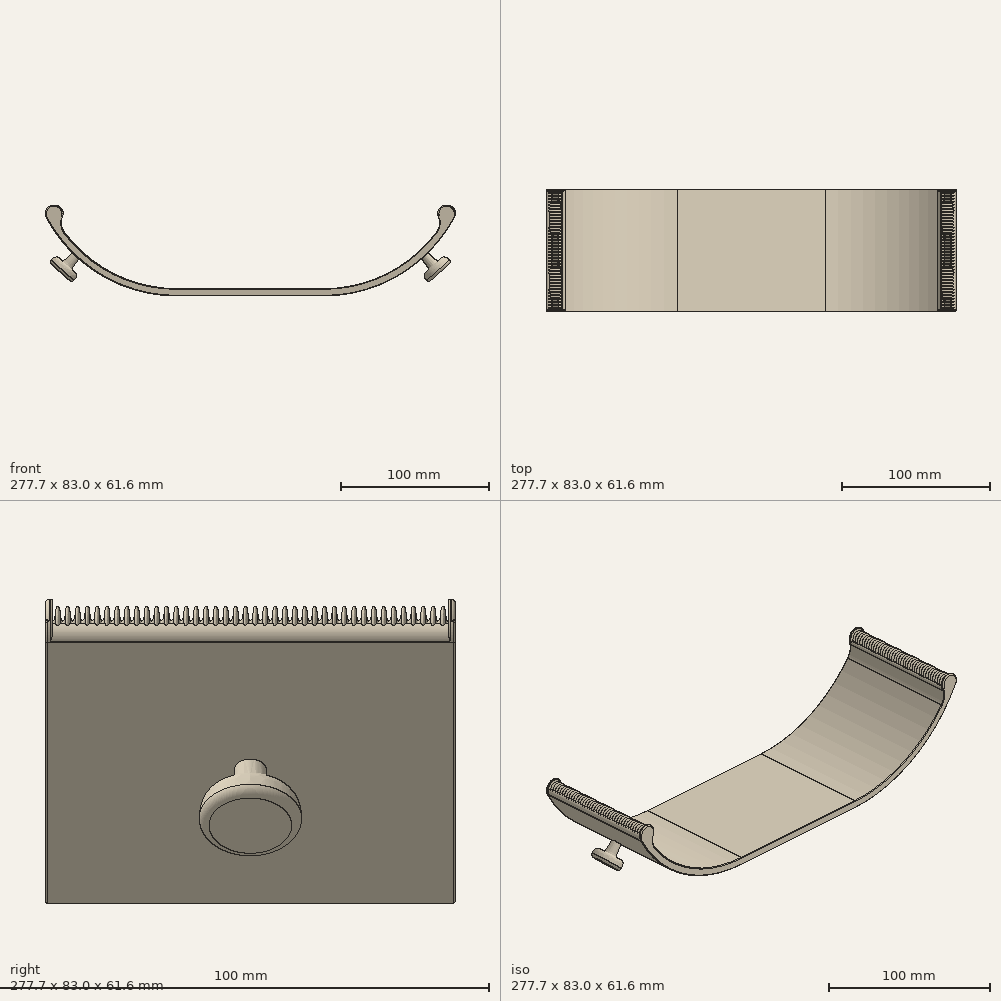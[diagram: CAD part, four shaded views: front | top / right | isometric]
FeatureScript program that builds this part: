
annotation { "Feature Type Name" : "Feature", "Feature Type Description" : "" }
export const myFeature = defineFeature(function(context is Context, id is Id, definition is map)
    precondition{}
    {
        {
            var Q0;
            Q0=qCreatedBy(makeId("Right.planeOp"),FACE);
            var sketch = newSketch(context, id + "F0", { "sketchPlane" : qUnion([Q0])});
            skLineSegment(sketch, "E0", {"start": v(1.5, 1.6) * mm, "end": v(1.5, 5.6) * mm});
            skLineSegment(sketch, "E1", {"start": v(1.1, 6) * mm, "end": v(0.8, 6) * mm});
            skLineSegment(sketch, "E2", {"start": v(0, 5.2) * mm, "end": v(0, 0) * mm});
            skLineSegment(sketch, "E3.top", {"start": v(81.9, 6) * mm, "end": v(82.2, 6) * mm});
            skLineSegment(sketch, "E3.right", {"start": v(83, 0) * mm, "end": v(83, 5.2) * mm});
            skArc(sketch, "E4.filletArc", {"start": v(81.9, 6) * mm, "mid": v(81.62, 5.88) * mm, "end": v(81.5, 5.6) * mm});
            skPoint(sketch, "E5.visualSharp", {"position": v(83, 6) * mm});
            skArc(sketch, "E5.filletArc", {"start": v(83, 5.2) * mm, "mid": v(82.77, 5.77) * mm, "end": v(82.2, 6) * mm});
            skArc(sketch, "E6.filletArc", {"start": v(1.5, 5.6) * mm, "mid": v(1.38, 5.88) * mm, "end": v(1.1, 6) * mm});
            skArc(sketch, "E7.filletArc", {"start": v(0.8, 6) * mm, "mid": v(0.23, 5.77) * mm, "end": v(0, 5.2) * mm});
            skEllipticalArc(sketch, "E8", {});
            skEllipticalArc(sketch, "E9", {});
            skEllipticalArc(sketch, "E10.MirrorCS", {});
            skEllipticalArc(sketch, "E11.MirrorCS", {});
            skLineSegment(sketch, "E12", {"start": v(81.5, 1.6) * mm, "end": v(81.5, 5.6) * mm});
            skEllipticalArc(sketch, "E13.1.0.0", {});
            skEllipticalArc(sketch, "E13.1.0.1", {});
            skEllipticalArc(sketch, "E13.1.0.2", {});
            skEllipticalArc(sketch, "E13.1.0.3", {});
            skEllipticalArc(sketch, "E13.2.0.0", {});
            skEllipticalArc(sketch, "E13.2.0.1", {});
            skEllipticalArc(sketch, "E13.2.0.2", {});
            skEllipticalArc(sketch, "E13.2.0.3", {});
            skEllipticalArc(sketch, "E13.3.0.0", {});
            skEllipticalArc(sketch, "E13.3.0.1", {});
            skEllipticalArc(sketch, "E13.3.0.2", {});
            skEllipticalArc(sketch, "E13.3.0.3", {});
            skEllipticalArc(sketch, "E13.4.0.0", {});
            skEllipticalArc(sketch, "E13.4.0.1", {});
            skEllipticalArc(sketch, "E13.4.0.2", {});
            skEllipticalArc(sketch, "E13.4.0.3", {});
            skEllipticalArc(sketch, "E13.5.0.0", {});
            skEllipticalArc(sketch, "E13.5.0.1", {});
            skEllipticalArc(sketch, "E13.5.0.2", {});
            skEllipticalArc(sketch, "E13.5.0.3", {});
            skEllipticalArc(sketch, "E13.6.0.0", {});
            skEllipticalArc(sketch, "E13.6.0.1", {});
            skEllipticalArc(sketch, "E13.6.0.2", {});
            skEllipticalArc(sketch, "E13.6.0.3", {});
            skEllipticalArc(sketch, "E13.7.0.0", {});
            skEllipticalArc(sketch, "E13.7.0.1", {});
            skEllipticalArc(sketch, "E13.7.0.2", {});
            skEllipticalArc(sketch, "E13.7.0.3", {});
            skEllipticalArc(sketch, "E13.8.0.0", {});
            skEllipticalArc(sketch, "E13.8.0.1", {});
            skEllipticalArc(sketch, "E13.8.0.2", {});
            skEllipticalArc(sketch, "E13.8.0.3", {});
            skEllipticalArc(sketch, "E13.9.0.0", {});
            skEllipticalArc(sketch, "E13.9.0.1", {});
            skEllipticalArc(sketch, "E13.9.0.2", {});
            skEllipticalArc(sketch, "E13.9.0.3", {});
            skEllipticalArc(sketch, "E13.10.0.0", {});
            skEllipticalArc(sketch, "E13.10.0.1", {});
            skEllipticalArc(sketch, "E13.10.0.2", {});
            skEllipticalArc(sketch, "E13.10.0.3", {});
            skEllipticalArc(sketch, "E13.11.0.0", {});
            skEllipticalArc(sketch, "E13.11.0.1", {});
            skEllipticalArc(sketch, "E13.11.0.2", {});
            skEllipticalArc(sketch, "E13.11.0.3", {});
            skEllipticalArc(sketch, "E13.12.0.0", {});
            skEllipticalArc(sketch, "E13.12.0.1", {});
            skEllipticalArc(sketch, "E13.12.0.2", {});
            skEllipticalArc(sketch, "E13.12.0.3", {});
            skEllipticalArc(sketch, "E13.13.0.0", {});
            skEllipticalArc(sketch, "E13.13.0.1", {});
            skEllipticalArc(sketch, "E13.13.0.2", {});
            skEllipticalArc(sketch, "E13.13.0.3", {});
            skEllipticalArc(sketch, "E13.14.0.0", {});
            skEllipticalArc(sketch, "E13.14.0.1", {});
            skEllipticalArc(sketch, "E13.14.0.2", {});
            skEllipticalArc(sketch, "E13.14.0.3", {});
            skEllipticalArc(sketch, "E13.15.0.0", {});
            skEllipticalArc(sketch, "E13.15.0.1", {});
            skEllipticalArc(sketch, "E13.15.0.2", {});
            skEllipticalArc(sketch, "E13.15.0.3", {});
            skEllipticalArc(sketch, "E13.16.0.0", {});
            skEllipticalArc(sketch, "E13.16.0.1", {});
            skEllipticalArc(sketch, "E13.16.0.2", {});
            skEllipticalArc(sketch, "E13.16.0.3", {});
            skEllipticalArc(sketch, "E13.17.0.0", {});
            skEllipticalArc(sketch, "E13.17.0.1", {});
            skEllipticalArc(sketch, "E13.17.0.2", {});
            skEllipticalArc(sketch, "E13.17.0.3", {});
            skEllipticalArc(sketch, "E13.18.0.0", {});
            skEllipticalArc(sketch, "E13.18.0.1", {});
            skEllipticalArc(sketch, "E13.18.0.2", {});
            skEllipticalArc(sketch, "E13.18.0.3", {});
            skEllipticalArc(sketch, "E13.19.0.0", {});
            skEllipticalArc(sketch, "E13.19.0.1", {});
            skEllipticalArc(sketch, "E13.19.0.2", {});
            skEllipticalArc(sketch, "E13.19.0.3", {});
            skEllipticalArc(sketch, "E13.20.0.0", {});
            skEllipticalArc(sketch, "E13.20.0.1", {});
            skEllipticalArc(sketch, "E13.20.0.2", {});
            skEllipticalArc(sketch, "E13.20.0.3", {});
            skEllipticalArc(sketch, "E13.21.0.0", {});
            skEllipticalArc(sketch, "E13.21.0.1", {});
            skEllipticalArc(sketch, "E13.21.0.2", {});
            skEllipticalArc(sketch, "E13.21.0.3", {});
            skEllipticalArc(sketch, "E13.22.0.0", {});
            skEllipticalArc(sketch, "E13.22.0.1", {});
            skEllipticalArc(sketch, "E13.22.0.2", {});
            skEllipticalArc(sketch, "E13.22.0.3", {});
            skEllipticalArc(sketch, "E13.23.0.0", {});
            skEllipticalArc(sketch, "E13.23.0.1", {});
            skEllipticalArc(sketch, "E13.23.0.2", {});
            skEllipticalArc(sketch, "E13.23.0.3", {});
            skEllipticalArc(sketch, "E13.24.0.0", {});
            skEllipticalArc(sketch, "E13.24.0.1", {});
            skEllipticalArc(sketch, "E13.24.0.2", {});
            skEllipticalArc(sketch, "E13.24.0.3", {});
            skEllipticalArc(sketch, "E13.25.0.0", {});
            skEllipticalArc(sketch, "E13.25.0.1", {});
            skEllipticalArc(sketch, "E13.25.0.2", {});
            skEllipticalArc(sketch, "E13.25.0.3", {});
            skEllipticalArc(sketch, "E13.26.0.0", {});
            skEllipticalArc(sketch, "E13.26.0.1", {});
            skEllipticalArc(sketch, "E13.26.0.2", {});
            skEllipticalArc(sketch, "E13.26.0.3", {});
            skEllipticalArc(sketch, "E13.27.0.0", {});
            skEllipticalArc(sketch, "E13.27.0.1", {});
            skEllipticalArc(sketch, "E13.27.0.2", {});
            skEllipticalArc(sketch, "E13.27.0.3", {});
            skEllipticalArc(sketch, "E13.28.0.0", {});
            skEllipticalArc(sketch, "E13.28.0.1", {});
            skEllipticalArc(sketch, "E13.28.0.2", {});
            skEllipticalArc(sketch, "E13.28.0.3", {});
            skEllipticalArc(sketch, "E13.29.0.0", {});
            skEllipticalArc(sketch, "E13.29.0.1", {});
            skEllipticalArc(sketch, "E13.29.0.2", {});
            skEllipticalArc(sketch, "E13.29.0.3", {});
            skEllipticalArc(sketch, "E13.30.0.0", {});
            skEllipticalArc(sketch, "E13.30.0.1", {});
            skEllipticalArc(sketch, "E13.30.0.2", {});
            skEllipticalArc(sketch, "E13.30.0.3", {});
            skEllipticalArc(sketch, "E13.31.0.0", {});
            skEllipticalArc(sketch, "E13.31.0.1", {});
            skEllipticalArc(sketch, "E13.31.0.2", {});
            skEllipticalArc(sketch, "E13.31.0.3", {});
            skEllipticalArc(sketch, "E13.32.0.0", {});
            skEllipticalArc(sketch, "E13.32.0.1", {});
            skEllipticalArc(sketch, "E13.32.0.2", {});
            skEllipticalArc(sketch, "E13.32.0.3", {});
            skEllipticalArc(sketch, "E13.33.0.0", {});
            skEllipticalArc(sketch, "E13.33.0.1", {});
            skEllipticalArc(sketch, "E13.33.0.2", {});
            skEllipticalArc(sketch, "E13.33.0.3", {});
            skEllipticalArc(sketch, "E13.34.0.0", {});
            skEllipticalArc(sketch, "E13.34.0.1", {});
            skEllipticalArc(sketch, "E13.34.0.2", {});
            skEllipticalArc(sketch, "E13.34.0.3", {});
            skEllipticalArc(sketch, "E13.35.0.0", {});
            skEllipticalArc(sketch, "E13.35.0.1", {});
            skEllipticalArc(sketch, "E13.35.0.2", {});
            skEllipticalArc(sketch, "E13.35.0.3", {});
            skEllipticalArc(sketch, "E13.36.0.0", {});
            skEllipticalArc(sketch, "E13.36.0.1", {});
            skEllipticalArc(sketch, "E13.36.0.2", {});
            skEllipticalArc(sketch, "E13.36.0.3", {});
            skEllipticalArc(sketch, "E13.37.0.0", {});
            skEllipticalArc(sketch, "E13.37.0.1", {});
            skEllipticalArc(sketch, "E13.37.0.2", {});
            skEllipticalArc(sketch, "E13.37.0.3", {});
            skEllipticalArc(sketch, "E13.38.0.0", {});
            skEllipticalArc(sketch, "E13.38.0.1", {});
            skEllipticalArc(sketch, "E13.38.0.2", {});
            skEllipticalArc(sketch, "E13.38.0.3", {});
            skEllipticalArc(sketch, "E13.39.0.0", {});
            skEllipticalArc(sketch, "E13.39.0.1", {});
            skEllipticalArc(sketch, "E13.39.0.2", {});
            skEllipticalArc(sketch, "E13.39.0.3", {});
            skLineSegment(sketch, "E13.direction1", {"start": v(1.5, 1.6) * mm, "end": v(3.5, 1.6) * mm, "construction": true});
            skLineSegment(sketch, "E14", {"start": v(0, 0) * mm, "end": v(83, 0) * mm});
            const initialGuessF0  = {"E8": [0.0015, 0.0031, 0, -1, 0.0015, 0.0005, 0, 1.5707963267948966], "E9": [0.0025, 0.0031, 0, 1, 0.0015, 0.0005, 0, 1.5707963267948966], "E10.MirrorCS": [0.0025, 0.0031, 0, 1, 0.0015, 0.0005, 4.71238898038469, 6.283185307179586], "E11.MirrorCS": [0.0035, 0.0031, 0, -1, 0.0015, 0.0005, 4.71238898038469, 0], "E13.1.0.0": [0.0045, 0.0031, 0, 1, 0.0015, 0.0005, 0, 1.5707963267948966], "E13.1.0.1": [0.0035, 0.0031, 0, -1, 0.0015, 0.0005, 0, 1.5707963267948966], "E13.1.0.2": [0.0045, 0.0031, 0, 1, 0.0015, 0.0005, 4.71238898038469, 0], "E13.1.0.3": [0.0055, 0.0031, 0, -1, 0.0015, 0.0005, 4.71238898038469, 0], "E13.2.0.0": [0.0065, 0.0031, 0, 1, 0.0015, 0.0005, 0, 1.5707963267948966], "E13.2.0.1": [0.0055, 0.0031, 0, -1, 0.0015, 0.0005, 0, 1.5707963267948966], "E13.2.0.2": [0.0065, 0.0031, 0, 1, 0.0015, 0.0005, 4.71238898038469, 0], "E13.2.0.3": [0.0075, 0.0031, 0, -1, 0.0015, 0.0005, 4.71238898038469, 0], "E13.3.0.0": [0.0085, 0.0031, 0, 1, 0.0015, 0.0005, 0, 1.5707963267948966], "E13.3.0.1": [0.0075, 0.0031, 0, -1, 0.0015, 0.0005, 0, 1.5707963267948966], "E13.3.0.2": [0.0085, 0.0031, 0, 1, 0.0015, 0.0005, 4.71238898038469, 0], "E13.3.0.3": [0.0095, 0.0031, 0, -1, 0.0015, 0.0005, 4.71238898038469, 0], "E13.4.0.0": [0.0105, 0.0031, 0, 1, 0.0015, 0.0005, 0, 1.5707963267948966], "E13.4.0.1": [0.0095, 0.0031, 0, -1, 0.0015, 0.0005, 0, 1.5707963267948966], "E13.4.0.2": [0.0105, 0.0031, 0, 1, 0.0015, 0.0005, 4.71238898038469, 0], "E13.4.0.3": [0.0115, 0.0031, 0, -1, 0.0015, 0.0005, 4.71238898038469, 0], "E13.5.0.0": [0.0125, 0.0031, 0, 1, 0.0015, 0.0005, 0, 1.5707963267948966], "E13.5.0.1": [0.0115, 0.0031, 0, -1, 0.0015, 0.0005, 0, 1.5707963267948966], "E13.5.0.2": [0.0125, 0.0031, 0, 1, 0.0015, 0.0005, 4.71238898038469, 0], "E13.5.0.3": [0.0135, 0.0031, 0, -1, 0.0015, 0.0005, 4.71238898038469, 0], "E13.6.0.0": [0.0145, 0.0031, 0, 1, 0.0015, 0.0005, 0, 1.5707963267948966], "E13.6.0.1": [0.0135, 0.0031, 0, -1, 0.0015, 0.0005, 0, 1.5707963267948966], "E13.6.0.2": [0.0145, 0.0031, 0, 1, 0.0015, 0.0005, 4.71238898038469, 0], "E13.6.0.3": [0.0155, 0.0031, 0, -1, 0.0015, 0.0005, 4.71238898038469, 0], "E13.7.0.0": [0.0165, 0.0031, 0, 1, 0.0015, 0.0005, 0, 1.5707963267948966], "E13.7.0.1": [0.0155, 0.0031, 0, -1, 0.0015, 0.0005, 0, 1.5707963267948966], "E13.7.0.2": [0.0165, 0.0031, 0, 1, 0.0015, 0.0005, 4.71238898038469, 0], "E13.7.0.3": [0.0175, 0.0031, 0, -1, 0.0015, 0.0005, 4.71238898038469, 0], "E13.8.0.0": [0.0185, 0.0031, 0, 1, 0.0015, 0.0005, 0, 1.5707963267948966], "E13.8.0.1": [0.0175, 0.0031, 0, -1, 0.0015, 0.0005, 0, 1.5707963267948966], "E13.8.0.2": [0.0185, 0.0031, 0, 1, 0.0015, 0.0005, 4.71238898038469, 0], "E13.8.0.3": [0.0195, 0.0031, 0, -1, 0.0015, 0.0005, 4.71238898038469, 0], "E13.9.0.0": [0.0205, 0.0031, 0, 1, 0.0015, 0.0005, 0, 1.5707963267948966], "E13.9.0.1": [0.0195, 0.0031, 0, -1, 0.0015, 0.0005, 0, 1.5707963267948966], "E13.9.0.2": [0.0205, 0.0031, 0, 1, 0.0015, 0.0005, 4.71238898038469, 0], "E13.9.0.3": [0.0215, 0.0031, 0, -1, 0.0015, 0.0005, 4.71238898038469, 0], "E13.10.0.0": [0.0225, 0.0031, 0, 1, 0.0015, 0.0005, 0, 1.5707963267948966], "E13.10.0.1": [0.0215, 0.0031, 0, -1, 0.0015, 0.0005, 0, 1.5707963267948966], "E13.10.0.2": [0.0225, 0.0031, 0, 1, 0.0015, 0.0005, 4.71238898038469, 0], "E13.10.0.3": [0.0235, 0.0031, 0, -1, 0.0015, 0.0005, 4.71238898038469, 0], "E13.11.0.0": [0.0245, 0.0031, 0, 1, 0.0015, 0.0005, 0, 1.5707963267948966], "E13.11.0.1": [0.0235, 0.0031, 0, -1, 0.0015, 0.0005, 0, 1.5707963267948966], "E13.11.0.2": [0.0245, 0.0031, 0, 1, 0.0015, 0.0005, 4.71238898038469, 0], "E13.11.0.3": [0.0255, 0.0031, 0, -1, 0.0015, 0.0005, 4.71238898038469, 0], "E13.12.0.0": [0.0265, 0.0031, 0, 1, 0.0015, 0.0005, 0, 1.5707963267948966], "E13.12.0.1": [0.0255, 0.0031, 0, -1, 0.0015, 0.0005, 0, 1.5707963267948966], "E13.12.0.2": [0.0265, 0.0031, 0, 1, 0.0015, 0.0005, 4.71238898038469, 0], "E13.12.0.3": [0.0275, 0.0031, 0, -1, 0.0015, 0.0005, 4.71238898038469, 0], "E13.13.0.0": [0.0285, 0.0031, 0, 1, 0.0015, 0.0005, 0, 1.5707963267948966], "E13.13.0.1": [0.0275, 0.0031, 0, -1, 0.0015, 0.0005, 0, 1.5707963267948966], "E13.13.0.2": [0.0285, 0.0031, 0, 1, 0.0015, 0.0005, 4.71238898038469, 0], "E13.13.0.3": [0.0295, 0.0031, 0, -1, 0.0015, 0.0005, 4.71238898038469, 0], "E13.14.0.0": [0.0305, 0.0031, 0, 1, 0.0015, 0.0005, 0, 1.5707963267948966], "E13.14.0.1": [0.0295, 0.0031, 0, -1, 0.0015, 0.0005, 0, 1.5707963267948966], "E13.14.0.2": [0.0305, 0.0031, 0, 1, 0.0015, 0.0005, 4.71238898038469, 0], "E13.14.0.3": [0.0315, 0.0031, 0, -1, 0.0015, 0.0005, 4.71238898038469, 0], "E13.15.0.0": [0.0325, 0.0031, 0, 1, 0.0015, 0.0005, 0, 1.5707963267948966], "E13.15.0.1": [0.0315, 0.0031, 0, -1, 0.0015, 0.0005, 0, 1.5707963267948966], "E13.15.0.2": [0.0325, 0.0031, 0, 1, 0.0015, 0.0005, 4.71238898038469, 0], "E13.15.0.3": [0.0335, 0.0031, 0, -1, 0.0015, 0.0005, 4.71238898038469, 0], "E13.16.0.0": [0.0345, 0.0031, 0, 1, 0.0015, 0.0005, 0, 1.5707963267948966], "E13.16.0.1": [0.0335, 0.0031, 0, -1, 0.0015, 0.0005, 0, 1.5707963267948966], "E13.16.0.2": [0.0345, 0.0031, 0, 1, 0.0015, 0.0005, 4.71238898038469, 0], "E13.16.0.3": [0.0355, 0.0031, 0, -1, 0.0015, 0.0005, 4.71238898038469, 0], "E13.17.0.0": [0.0365, 0.0031, 0, 1, 0.0015, 0.0005, 0, 1.5707963267948966], "E13.17.0.1": [0.0355, 0.0031, 0, -1, 0.0015, 0.0005, 0, 1.5707963267948966], "E13.17.0.2": [0.0365, 0.0031, 0, 1, 0.0015, 0.0005, 4.71238898038469, 0], "E13.17.0.3": [0.0375, 0.0031, 0, -1, 0.0015, 0.0005, 4.71238898038469, 0], "E13.18.0.0": [0.0385, 0.0031, 0, 1, 0.0015, 0.0005, 0, 1.5707963267948966], "E13.18.0.1": [0.0375, 0.0031, 0, -1, 0.0015, 0.0005, 0, 1.5707963267948966], "E13.18.0.2": [0.0385, 0.0031, 0, 1, 0.0015, 0.0005, 4.71238898038469, 0], "E13.18.0.3": [0.0395, 0.0031, 0, -1, 0.0015, 0.0005, 4.71238898038469, 0], "E13.19.0.0": [0.0405, 0.0031, 0, 1, 0.0015, 0.0005, 0, 1.5707963267948966], "E13.19.0.1": [0.0395, 0.0031, 0, -1, 0.0015, 0.0005, 0, 1.5707963267948966], "E13.19.0.2": [0.0405, 0.0031, 0, 1, 0.0015, 0.0005, 4.71238898038469, 0], "E13.19.0.3": [0.0415, 0.0031, 0, -1, 0.0015, 0.0005, 4.71238898038469, 0], "E13.20.0.0": [0.0425, 0.0031, 0, 1, 0.0015, 0.0005, 0, 1.5707963267948966], "E13.20.0.1": [0.0415, 0.0031, 0, -1, 0.0015, 0.0005, 0, 1.5707963267948966], "E13.20.0.2": [0.0425, 0.0031, 0, 1, 0.0015, 0.0005, 4.71238898038469, 0], "E13.20.0.3": [0.0435, 0.0031, 0, -1, 0.0015, 0.0005, 4.71238898038469, 0], "E13.21.0.0": [0.0445, 0.0031, 0, 1, 0.0015, 0.0005, 0, 1.5707963267948966], "E13.21.0.1": [0.0435, 0.0031, 0, -1, 0.0015, 0.0005, 0, 1.5707963267948966], "E13.21.0.2": [0.0445, 0.0031, 0, 1, 0.0015, 0.0005, 4.71238898038469, 0], "E13.21.0.3": [0.0455, 0.0031, 0, -1, 0.0015, 0.0005, 4.71238898038469, 0], "E13.22.0.0": [0.0465, 0.0031, 0, 1, 0.0015, 0.0005, 0, 1.5707963267948966], "E13.22.0.1": [0.0455, 0.0031, 0, -1, 0.0015, 0.0005, 0, 1.5707963267948966], "E13.22.0.2": [0.0465, 0.0031, 0, 1, 0.0015, 0.0005, 4.71238898038469, 0], "E13.22.0.3": [0.0475, 0.0031, 0, -1, 0.0015, 0.0005, 4.71238898038469, 0], "E13.23.0.0": [0.0485, 0.0031, 0, 1, 0.0015, 0.0005, 0, 1.5707963267948966], "E13.23.0.1": [0.0475, 0.0031, 0, -1, 0.0015, 0.0005, 0, 1.5707963267948966], "E13.23.0.2": [0.0485, 0.0031, 0, 1, 0.0015, 0.0005, 4.71238898038469, 0], "E13.23.0.3": [0.0495, 0.0031, 0, -1, 0.0015, 0.0005, 4.71238898038469, 0], "E13.24.0.0": [0.0505, 0.0031, 0, 1, 0.0015, 0.0005, 0, 1.5707963267948966], "E13.24.0.1": [0.0495, 0.0031, 0, -1, 0.0015, 0.0005, 0, 1.5707963267948966], "E13.24.0.2": [0.0505, 0.0031, 0, 1, 0.0015, 0.0005, 4.71238898038469, 0], "E13.24.0.3": [0.0515, 0.0031, 0, -1, 0.0015, 0.0005, 4.71238898038469, 0], "E13.25.0.0": [0.0525, 0.0031, 0, 1, 0.0015, 0.0005, 0, 1.5707963267948966], "E13.25.0.1": [0.0515, 0.0031, 0, -1, 0.0015, 0.0005, 0, 1.5707963267948966], "E13.25.0.2": [0.0525, 0.0031, 0, 1, 0.0015, 0.0005, 4.71238898038469, 0], "E13.25.0.3": [0.0535, 0.0031, 0, -1, 0.0015, 0.0005, 4.71238898038469, 0], "E13.26.0.0": [0.0545, 0.0031, 0, 1, 0.0015, 0.0005, 0, 1.5707963267948966], "E13.26.0.1": [0.0535, 0.0031, 0, -1, 0.0015, 0.0005, 0, 1.5707963267948966], "E13.26.0.2": [0.0545, 0.0031, 0, 1, 0.0015, 0.0005, 4.71238898038469, 0], "E13.26.0.3": [0.0555, 0.0031, 0, -1, 0.0015, 0.0005, 4.71238898038469, 0], "E13.27.0.0": [0.0565, 0.0031, 0, 1, 0.0015, 0.0005, 0, 1.5707963267948966], "E13.27.0.1": [0.0555, 0.0031, 0, -1, 0.0015, 0.0005, 0, 1.5707963267948966], "E13.27.0.2": [0.0565, 0.0031, 0, 1, 0.0015, 0.0005, 4.71238898038469, 0], "E13.27.0.3": [0.0575, 0.0031, 0, -1, 0.0015, 0.0005, 4.71238898038469, 0], "E13.28.0.0": [0.0585, 0.0031, 0, 1, 0.0015, 0.0005, 0, 1.5707963267948966], "E13.28.0.1": [0.0575, 0.0031, 0, -1, 0.0015, 0.0005, 0, 1.5707963267948966], "E13.28.0.2": [0.0585, 0.0031, 0, 1, 0.0015, 0.0005, 4.71238898038469, 0], "E13.28.0.3": [0.0595, 0.0031, 0, -1, 0.0015, 0.0005, 4.71238898038469, 0], "E13.29.0.0": [0.0605, 0.0031, 0, 1, 0.0015, 0.0005, 0, 1.5707963267948966], "E13.29.0.1": [0.0595, 0.0031, 0, -1, 0.0015, 0.0005, 0, 1.5707963267948966], "E13.29.0.2": [0.0605, 0.0031, 0, 1, 0.0015, 0.0005, 4.71238898038469, 0], "E13.29.0.3": [0.0615, 0.0031, 0, -1, 0.0015, 0.0005, 4.71238898038469, 0], "E13.30.0.0": [0.0625, 0.0031, 0, 1, 0.0015, 0.0005, 0, 1.5707963267948966], "E13.30.0.1": [0.0615, 0.0031, 0, -1, 0.0015, 0.0005, 0, 1.5707963267948966], "E13.30.0.2": [0.0625, 0.0031, 0, 1, 0.0015, 0.0005, 4.71238898038469, 0], "E13.30.0.3": [0.0635, 0.0031, 0, -1, 0.0015, 0.0005, 4.71238898038469, 0], "E13.31.0.0": [0.0645, 0.0031, 0, 1, 0.0015, 0.0005, 0, 1.5707963267948966], "E13.31.0.1": [0.0635, 0.0031, 0, -1, 0.0015, 0.0005, 0, 1.5707963267948966], "E13.31.0.2": [0.0645, 0.0031, 0, 1, 0.0015, 0.0005, 4.71238898038469, 0], "E13.31.0.3": [0.0655, 0.0031, 0, -1, 0.0015, 0.0005, 4.71238898038469, 0], "E13.32.0.0": [0.0665, 0.0031, 0, 1, 0.0015, 0.0005, 0, 1.5707963267948966], "E13.32.0.1": [0.0655, 0.0031, 0, -1, 0.0015, 0.0005, 0, 1.5707963267948966], "E13.32.0.2": [0.0665, 0.0031, 0, 1, 0.0015, 0.0005, 4.71238898038469, 0], "E13.32.0.3": [0.0675, 0.0031, 0, -1, 0.0015, 0.0005, 4.71238898038469, 0], "E13.33.0.0": [0.0685, 0.0031, 0, 1, 0.0015, 0.0005, 0, 1.5707963267948966], "E13.33.0.1": [0.0675, 0.0031, 0, -1, 0.0015, 0.0005, 0, 1.5707963267948966], "E13.33.0.2": [0.0685, 0.0031, 0, 1, 0.0015, 0.0005, 4.71238898038469, 0], "E13.33.0.3": [0.0695, 0.0031, 0, -1, 0.0015, 0.0005, 4.71238898038469, 0], "E13.34.0.0": [0.0705, 0.0031, 0, 1, 0.0015, 0.0005, 0, 1.5707963267948966], "E13.34.0.1": [0.0695, 0.0031, 0, -1, 0.0015, 0.0005, 0, 1.5707963267948966], "E13.34.0.2": [0.0705, 0.0031, 0, 1, 0.0015, 0.0005, 4.71238898038469, 0], "E13.34.0.3": [0.0715, 0.0031, 0, -1, 0.0015, 0.0005, 4.71238898038469, 0], "E13.35.0.0": [0.0725, 0.0031, 0, 1, 0.0015, 0.0005, 0, 1.5707963267948966], "E13.35.0.1": [0.0715, 0.0031, 0, -1, 0.0015, 0.0005, 0, 1.5707963267948966], "E13.35.0.2": [0.0725, 0.0031, 0, 1, 0.0015, 0.0005, 4.71238898038469, 0], "E13.35.0.3": [0.0735, 0.0031, 0, -1, 0.0015, 0.0005, 4.71238898038469, 0], "E13.36.0.0": [0.0745, 0.0031, 0, 1, 0.0015, 0.0005, 0, 1.5707963267948966], "E13.36.0.1": [0.0735, 0.0031, 0, -1, 0.0015, 0.0005, 0, 1.5707963267948966], "E13.36.0.2": [0.0745, 0.0031, 0, 1, 0.0015, 0.0005, 4.71238898038469, 0], "E13.36.0.3": [0.0755, 0.0031, 0, -1, 0.0015, 0.0005, 4.71238898038469, 0], "E13.37.0.0": [0.0765, 0.0031, 0, 1, 0.0015, 0.0005, 0, 1.5707963267948966], "E13.37.0.1": [0.0755, 0.0031, 0, -1, 0.0015, 0.0005, 0, 1.5707963267948966], "E13.37.0.2": [0.0765, 0.0031, 0, 1, 0.0015, 0.0005, 4.71238898038469, 0], "E13.37.0.3": [0.0775, 0.0031, 0, -1, 0.0015, 0.0005, 4.71238898038469, 0], "E13.38.0.0": [0.0785, 0.0031, 0, 1, 0.0015, 0.0005, 0, 1.5707963267948966], "E13.38.0.1": [0.0775, 0.0031, 0, -1, 0.0015, 0.0005, 0, 1.5707963267948966], "E13.38.0.2": [0.0785, 0.0031, 0, 1, 0.0015, 0.0005, 4.71238898038469, 0], "E13.38.0.3": [0.0795, 0.0031, 0, -1, 0.0015, 0.0005, 4.71238898038469, 0], "E13.39.0.0": [0.0805, 0.0031, 0, 1, 0.0015, 0.0005, 0, 1.5707963267948966], "E13.39.0.1": [0.0795, 0.0031, 0, -1, 0.0015, 0.0005, 0, 1.5707963267948966], "E13.39.0.2": [0.0805, 0.0031, 0, 1, 0.0015, 0.0005, 4.71238898038469, 0], "E13.39.0.3": [0.0815, 0.0031, 0, -1, 0.0015, 0.0005, 4.71238898038469, 0]};
            skSetInitialGuess(sketch, initialGuessF0);
            skSolve(sketch);
        }
        {
            var Q0;
            Q0=makeQuery(id+"F0.imprint","IMPRINT",FACE,{"disambiguationData":[TD([[makeQuery(id+"F0.imprint","IMPRINT",EDGE,{"derivedFrom":sQuery(id+"F0.wireOp",EDGE,"E0")}),1.0]])]});
            var Q1;
            Q1=sQuery(id+"F0.wireOp",EDGE,"E14");
            revolve(context, id + "F1", {"entities" : qUnion([Q0]), "axis" : qUnion([Q1]), "revolveType" : RevolveType.FULL});
        }
        {
            var Q0;
            Q0=qCreatedBy(makeId("Front.planeOp"),FACE);
            var sketch = newSketch(context, id + "F2", { "sketchPlane" : qUnion([Q0])});
            skArc(sketch, "E15", {"start": v(-5.29, -2.83) * mm, "mid": v(31.49, -41.4) * mm, "end": v(82.85, -55.6) * mm});
            skLineSegment(sketch, "E16", {"start": v(82.85, -55.6) * mm, "end": v(132.85, -55.6) * mm});
            skLineSegment(sketch, "E17.0", {"start": v(82.85, -50.6) * mm, "end": v(132.85, -50.6) * mm});
            skArc(sketch, "E17.1", {"start": v(7.1, -12.92) * mm, "mid": v(40.55, -40.66) * mm, "end": v(82.85, -50.6) * mm});
            skLineSegment(sketch, "E18", {"start": v(132.85, -50.6) * mm, "end": v(132.85, -55.6) * mm});
            skCircle(sketch, "E19.0", {"center": v(0, 0) * mm, "radius": 6 * mm, "construction": true});
            skArc(sketch, "E20", {"start": v(5.6, -2.17) * mm, "mid": v(4.95, -7.74) * mm, "end": v(7.1, -12.92) * mm});
            skLineSegment(sketch, "E21", {"start": v(5.6, -2.17) * mm, "end": v(-5.6, 2.17) * mm});
            skArc(sketch, "E22", {"start": v(-5.6, 2.17) * mm, "mid": v(-5.99, -0.36) * mm, "end": v(-5.29, -2.83) * mm});
            skSolve(sketch);
        }
        {
            var Q0;
            Q0=makeQuery(id+"F2.imprint","IMPRINT",FACE,{"disambiguationData":[TD([[makeQuery(id+"F2.imprint","IMPRINT",EDGE,{"derivedFrom":sQuery(id+"F2.wireOp",EDGE,"E15")}),1.0]])]});
            extrude(context, id + "F3", {"entities" : qUnion([Q0]), "operationType" : NewBodyOperationType.ADD, "oppositeDirection" : true, "depth" : 83 * mm});
        }
        {
            var Q0;
            {var subQ0=sQuery(id+"F2.wireOp",EDGE,"E20");var subQ1=makeQuery(id+"F3.opExtrude","SWEPT_FACE",FACE,{"disambiguationData":[OSD([subQ0])]});var subQ3=sQuery(id+"F2.wireOp",EDGE,"E21");var subQ4=makeQuery(id+"F3.opExtrude","SWEPT_FACE",FACE,{"disambiguationData":[OSD([subQ3])]});Q0=makeQuery(id+"F3.boolean.opBoolean","SPLIT",EDGE,{"disambiguationData":[topologyDisambiguationEdgeConnected([subQ1,subQ4]),TD([makeQuery(id+"F1.opRevolve","SWEPT_FACE",FACE,{"disambiguationData":[OSD([sQuery(id+"F0.wireOp",EDGE,"E2")])]})])],"derivedFrom":makeQuery(id+"F3.opExtrude","SWEPT_EDGE",EDGE,{"disambiguationData":[OSD([subQ0,subQ3])]})});}
            var Q1;
            {var subQ0=sQuery(id+"F2.wireOp",EDGE,"E22");var subQ1=sQuery(id+"F2.wireOp",EDGE,"E21");Q1=makeQuery(id+"F3.boolean.opBoolean","SPLIT",EDGE,{"disambiguationData":[TD([makeQuery(id+"F1.opRevolve","SWEPT_FACE",FACE,{"disambiguationData":[OSD([sQuery(id+"F0.wireOp",EDGE,"E2")])]})])],"derivedFrom":makeQuery(id+"F3.opExtrude","SWEPT_EDGE",EDGE,{"disambiguationData":[OSD([subQ1,subQ0])]})});}
            var Q2;
            {var subQ0=sQuery(id+"F2.wireOp",EDGE,"E22");var subQ1=sQuery(id+"F2.wireOp",EDGE,"E21");Q2=makeQuery(id+"F3.boolean.opBoolean","SPLIT",EDGE,{"disambiguationData":[TD([makeQuery(id+"F1.opRevolve","SWEPT_FACE",FACE,{"disambiguationData":[OSD([sQuery(id+"F0.wireOp",EDGE,"E3.right")])]})])],"derivedFrom":makeQuery(id+"F3.opExtrude","SWEPT_EDGE",EDGE,{"disambiguationData":[OSD([subQ1,subQ0])]})});}
            var Q3;
            {var subQ1=sQuery(id+"F2.wireOp",EDGE,"E21");var subQ2=sQuery(id+"F2.wireOp",EDGE,"E20");var subQ3=makeQuery(id+"F3.opExtrude","SWEPT_FACE",FACE,{"disambiguationData":[OSD([subQ2])]});var subQ4=makeQuery(id+"F3.opExtrude","SWEPT_FACE",FACE,{"disambiguationData":[OSD([subQ1])]});Q3=makeQuery(id+"F3.boolean.opBoolean","SPLIT",EDGE,{"disambiguationData":[topologyDisambiguationEdgeConnected([subQ3,subQ4]),TD([makeQuery(id+"F1.opRevolve","SWEPT_FACE",FACE,{"disambiguationData":[OSD([sQuery(id+"F0.wireOp",EDGE,"E3.right")])]})])],"derivedFrom":makeQuery(id+"F3.opExtrude","SWEPT_EDGE",EDGE,{"disambiguationData":[OSD([subQ2,subQ1])]})});}
            fillet(context, id + "F4", {"entities" : qUnion([Q0, Q1, Q2, Q3]), "radius" : 0.7 * mm, "tangentPropagation" : true, "allowEdgeOverflow" : false});
        }
        {
            var Q0;
            {var subQ0=sQuery(id+"F2.wireOp",EDGE,"E20");var subQ1=makeQuery(id+"F3.opExtrude","SWEPT_FACE",FACE,{"disambiguationData":[OSD([subQ0])]});var subQ2=sQuery(id+"F2.wireOp",EDGE,"E21");var subQ3=makeQuery(id+"F3.opExtrude","SWEPT_FACE",FACE,{"disambiguationData":[OSD([subQ2])]});Q0=makeQuery(id+"F3.boolean.opBoolean","SPLIT",EDGE,{"disambiguationData":[topologyDisambiguationEdgeConnected([subQ1,subQ3]),TD([makeQuery(id+"F1.opRevolve","SWEPT_FACE",FACE,{"disambiguationData":[OSD([sQuery(id+"F0.wireOp",EDGE,"E4.filletArc")])]})])],"derivedFrom":makeQuery(id+"F3.opExtrude","SWEPT_EDGE",EDGE,{"disambiguationData":[OSD([subQ0,subQ2])]})});}
            fillet(context, id + "F5", {"entities" : qUnion([Q0]), "radius" : 2 * mm, "tangentPropagation" : true, "allowEdgeOverflow" : false});
        }
        {
            var Q0;
            {var subQ0=sQuery(id+"F2.wireOp",EDGE,"E21");var subQ1=sQuery(id+"F2.wireOp",EDGE,"E22");Q0=makeQuery(id+"F3.boolean.opBoolean","SPLIT",EDGE,{"disambiguationData":[TD([makeQuery(id+"F1.opRevolve","SWEPT_FACE",FACE,{"disambiguationData":[OSD([sQuery(id+"F0.wireOp",EDGE,"E4.filletArc")])]})])],"derivedFrom":makeQuery(id+"F3.opExtrude","SWEPT_EDGE",EDGE,{"disambiguationData":[OSD([subQ0,subQ1])]})});}
            fillet(context, id + "F6", {"entities" : qUnion([Q0]), "radius" : 2.5 * mm, "tangentPropagation" : true, "allowEdgeOverflow" : false});
        }
        {
            var Q0;
            Q0=qCreatedBy(makeId("Front.planeOp"),FACE);
            cPlane(context, id + "F7", {"entities" : qUnion([Q0]), "cplaneType" : CPlaneType.OFFSET, "offset" : 41.5 * mm, "oppositeDirection" : true, "width" : 150 * mm, "height" : 150 * mm});
        }
        {
            var Q0;
            Q0=qCreatedBy(id+"F7.planeOp",FACE);
            var sketch = newSketch(context, id + "F8", { "sketchPlane" : qUnion([Q0])});
            skArc(sketch, "E23.0", {"start": v(-5.29, -2.83) * mm, "mid": v(31.49, -41.4) * mm, "end": v(82.85, -55.6) * mm, "construction": true});
            skLineSegment(sketch, "E24", {"start": v(15.9, -27) * mm, "end": v(4.43, -39.84) * mm});
            skLineSegment(sketch, "E25", {"start": v(13.54, -24.8) * mm, "end": v(15.9, -27) * mm});
            skLineSegment(sketch, "E26", {"start": v(4.43, -39.84) * mm, "end": v(-1.82, -34.26) * mm});
            skFitSpline(sketch, "E27", {"points": [v(13.54, -24.8) * mm, v(3.71, -33.2) * mm, v(3.3, -30.25) * mm, v(-3.2, -33.04) * mm], "startDerivative": vector(-22.65, -26.75) * mm, "endDerivative": vector(-28.75, -42.72) * mm});
            skArc(sketch, "E28.filletArc", {"start": v(-2, -31.46) * mm, "mid": v(-2.49, -32.9) * mm, "end": v(-1.82, -34.26) * mm});
            skSolve(sketch);
        }
        {
            var Q0;
            Q0=makeQuery(id+"F8.imprint","IMPRINT",FACE,{"disambiguationData":[TD([[makeQuery(id+"F8.imprint","IMPRINT",EDGE,{"derivedFrom":sQuery(id+"F8.wireOp",EDGE,"E24")}),-1.0]])]});
            var Q1;
            Q1=sQuery(id+"F8.wireOp",EDGE,"E24");
            revolve(context, id + "F9", {"operationType" : NewBodyOperationType.ADD, "entities" : qUnion([Q0]), "axis" : qUnion([Q1]), "revolveType" : RevolveType.FULL});
        }
        {
            var Q0;
            Q0=makeQuery(id+"F1.opRevolve","SWEPT_BODY",BODY,{"disambiguationData":[OSD([sQuery(id+"F0.wireOp",EDGE,"E0"),sQuery(id+"F0.wireOp",EDGE,"E1"),sQuery(id+"F0.wireOp",EDGE,"E2"),sQuery(id+"F0.wireOp",EDGE,"E3.top"),sQuery(id+"F0.wireOp",EDGE,"E3.right"),sQuery(id+"F0.wireOp",EDGE,"E4.filletArc"),sQuery(id+"F0.wireOp",EDGE,"E5.filletArc"),sQuery(id+"F0.wireOp",EDGE,"E6.filletArc"),sQuery(id+"F0.wireOp",EDGE,"E7.filletArc"),sQuery(id+"F0.wireOp",EDGE,"E8"),sQuery(id+"F0.wireOp",EDGE,"E9"),sQuery(id+"F0.wireOp",EDGE,"E10.MirrorCS"),sQuery(id+"F0.wireOp",EDGE,"E11.MirrorCS"),sQuery(id+"F0.wireOp",EDGE,"E12"),sQuery(id+"F0.wireOp",EDGE,"E13.1.0.0"),sQuery(id+"F0.wireOp",EDGE,"E13.1.0.1"),sQuery(id+"F0.wireOp",EDGE,"E13.1.0.2"),sQuery(id+"F0.wireOp",EDGE,"E13.1.0.3"),sQuery(id+"F0.wireOp",EDGE,"E13.2.0.0"),sQuery(id+"F0.wireOp",EDGE,"E13.2.0.1"),sQuery(id+"F0.wireOp",EDGE,"E13.2.0.2"),sQuery(id+"F0.wireOp",EDGE,"E13.2.0.3"),sQuery(id+"F0.wireOp",EDGE,"E13.3.0.0"),sQuery(id+"F0.wireOp",EDGE,"E13.3.0.1"),sQuery(id+"F0.wireOp",EDGE,"E13.3.0.2"),sQuery(id+"F0.wireOp",EDGE,"E13.3.0.3"),sQuery(id+"F0.wireOp",EDGE,"E13.4.0.0"),sQuery(id+"F0.wireOp",EDGE,"E13.4.0.1"),sQuery(id+"F0.wireOp",EDGE,"E13.4.0.2"),sQuery(id+"F0.wireOp",EDGE,"E13.4.0.3"),sQuery(id+"F0.wireOp",EDGE,"E13.5.0.0"),sQuery(id+"F0.wireOp",EDGE,"E13.5.0.1"),sQuery(id+"F0.wireOp",EDGE,"E13.5.0.2"),sQuery(id+"F0.wireOp",EDGE,"E13.5.0.3"),sQuery(id+"F0.wireOp",EDGE,"E13.6.0.0"),sQuery(id+"F0.wireOp",EDGE,"E13.6.0.1"),sQuery(id+"F0.wireOp",EDGE,"E13.6.0.2"),sQuery(id+"F0.wireOp",EDGE,"E13.6.0.3"),sQuery(id+"F0.wireOp",EDGE,"E13.7.0.0"),sQuery(id+"F0.wireOp",EDGE,"E13.7.0.1"),sQuery(id+"F0.wireOp",EDGE,"E13.7.0.2"),sQuery(id+"F0.wireOp",EDGE,"E13.7.0.3"),sQuery(id+"F0.wireOp",EDGE,"E13.8.0.0"),sQuery(id+"F0.wireOp",EDGE,"E13.8.0.1"),sQuery(id+"F0.wireOp",EDGE,"E13.8.0.2"),sQuery(id+"F0.wireOp",EDGE,"E13.8.0.3"),sQuery(id+"F0.wireOp",EDGE,"E13.9.0.0"),sQuery(id+"F0.wireOp",EDGE,"E13.9.0.1"),sQuery(id+"F0.wireOp",EDGE,"E13.9.0.2"),sQuery(id+"F0.wireOp",EDGE,"E13.9.0.3"),sQuery(id+"F0.wireOp",EDGE,"E13.10.0.0"),sQuery(id+"F0.wireOp",EDGE,"E13.10.0.1"),sQuery(id+"F0.wireOp",EDGE,"E13.10.0.2"),sQuery(id+"F0.wireOp",EDGE,"E13.10.0.3"),sQuery(id+"F0.wireOp",EDGE,"E13.11.0.0"),sQuery(id+"F0.wireOp",EDGE,"E13.11.0.1"),sQuery(id+"F0.wireOp",EDGE,"E13.11.0.2"),sQuery(id+"F0.wireOp",EDGE,"E13.11.0.3"),sQuery(id+"F0.wireOp",EDGE,"E13.12.0.0"),sQuery(id+"F0.wireOp",EDGE,"E13.12.0.1"),sQuery(id+"F0.wireOp",EDGE,"E13.12.0.2"),sQuery(id+"F0.wireOp",EDGE,"E13.12.0.3"),sQuery(id+"F0.wireOp",EDGE,"E13.13.0.0"),sQuery(id+"F0.wireOp",EDGE,"E13.13.0.1"),sQuery(id+"F0.wireOp",EDGE,"E13.13.0.2"),sQuery(id+"F0.wireOp",EDGE,"E13.13.0.3"),sQuery(id+"F0.wireOp",EDGE,"E13.14.0.0"),sQuery(id+"F0.wireOp",EDGE,"E13.14.0.1"),sQuery(id+"F0.wireOp",EDGE,"E13.14.0.2"),sQuery(id+"F0.wireOp",EDGE,"E13.14.0.3"),sQuery(id+"F0.wireOp",EDGE,"E13.15.0.0"),sQuery(id+"F0.wireOp",EDGE,"E13.15.0.1"),sQuery(id+"F0.wireOp",EDGE,"E13.15.0.2"),sQuery(id+"F0.wireOp",EDGE,"E13.15.0.3"),sQuery(id+"F0.wireOp",EDGE,"E13.16.0.0"),sQuery(id+"F0.wireOp",EDGE,"E13.16.0.1"),sQuery(id+"F0.wireOp",EDGE,"E13.16.0.2"),sQuery(id+"F0.wireOp",EDGE,"E13.16.0.3"),sQuery(id+"F0.wireOp",EDGE,"E13.17.0.0"),sQuery(id+"F0.wireOp",EDGE,"E13.17.0.1"),sQuery(id+"F0.wireOp",EDGE,"E13.17.0.2"),sQuery(id+"F0.wireOp",EDGE,"E13.17.0.3"),sQuery(id+"F0.wireOp",EDGE,"E13.18.0.0"),sQuery(id+"F0.wireOp",EDGE,"E13.18.0.1"),sQuery(id+"F0.wireOp",EDGE,"E13.18.0.2"),sQuery(id+"F0.wireOp",EDGE,"E13.18.0.3"),sQuery(id+"F0.wireOp",EDGE,"E13.19.0.0"),sQuery(id+"F0.wireOp",EDGE,"E13.19.0.1"),sQuery(id+"F0.wireOp",EDGE,"E13.19.0.2"),sQuery(id+"F0.wireOp",EDGE,"E13.19.0.3"),sQuery(id+"F0.wireOp",EDGE,"E13.20.0.0"),sQuery(id+"F0.wireOp",EDGE,"E13.20.0.1"),sQuery(id+"F0.wireOp",EDGE,"E13.20.0.2"),sQuery(id+"F0.wireOp",EDGE,"E13.20.0.3"),sQuery(id+"F0.wireOp",EDGE,"E13.21.0.0"),sQuery(id+"F0.wireOp",EDGE,"E13.21.0.1"),sQuery(id+"F0.wireOp",EDGE,"E13.21.0.2"),sQuery(id+"F0.wireOp",EDGE,"E13.21.0.3"),sQuery(id+"F0.wireOp",EDGE,"E13.22.0.0"),sQuery(id+"F0.wireOp",EDGE,"E13.22.0.1"),sQuery(id+"F0.wireOp",EDGE,"E13.22.0.2"),sQuery(id+"F0.wireOp",EDGE,"E13.22.0.3"),sQuery(id+"F0.wireOp",EDGE,"E13.23.0.0"),sQuery(id+"F0.wireOp",EDGE,"E13.23.0.1"),sQuery(id+"F0.wireOp",EDGE,"E13.23.0.2"),sQuery(id+"F0.wireOp",EDGE,"E13.23.0.3"),sQuery(id+"F0.wireOp",EDGE,"E13.24.0.0"),sQuery(id+"F0.wireOp",EDGE,"E13.24.0.1"),sQuery(id+"F0.wireOp",EDGE,"E13.24.0.2"),sQuery(id+"F0.wireOp",EDGE,"E13.24.0.3"),sQuery(id+"F0.wireOp",EDGE,"E13.25.0.0"),sQuery(id+"F0.wireOp",EDGE,"E13.25.0.1"),sQuery(id+"F0.wireOp",EDGE,"E13.25.0.2"),sQuery(id+"F0.wireOp",EDGE,"E13.25.0.3"),sQuery(id+"F0.wireOp",EDGE,"E13.26.0.0"),sQuery(id+"F0.wireOp",EDGE,"E13.26.0.1"),sQuery(id+"F0.wireOp",EDGE,"E13.26.0.2"),sQuery(id+"F0.wireOp",EDGE,"E13.26.0.3"),sQuery(id+"F0.wireOp",EDGE,"E13.27.0.0"),sQuery(id+"F0.wireOp",EDGE,"E13.27.0.1"),sQuery(id+"F0.wireOp",EDGE,"E13.27.0.2"),sQuery(id+"F0.wireOp",EDGE,"E13.27.0.3"),sQuery(id+"F0.wireOp",EDGE,"E13.28.0.0"),sQuery(id+"F0.wireOp",EDGE,"E13.28.0.1"),sQuery(id+"F0.wireOp",EDGE,"E13.28.0.2"),sQuery(id+"F0.wireOp",EDGE,"E13.28.0.3"),sQuery(id+"F0.wireOp",EDGE,"E13.29.0.0"),sQuery(id+"F0.wireOp",EDGE,"E13.29.0.1"),sQuery(id+"F0.wireOp",EDGE,"E13.29.0.2"),sQuery(id+"F0.wireOp",EDGE,"E13.29.0.3"),sQuery(id+"F0.wireOp",EDGE,"E13.30.0.0"),sQuery(id+"F0.wireOp",EDGE,"E13.30.0.1"),sQuery(id+"F0.wireOp",EDGE,"E13.30.0.2"),sQuery(id+"F0.wireOp",EDGE,"E13.30.0.3"),sQuery(id+"F0.wireOp",EDGE,"E13.31.0.0"),sQuery(id+"F0.wireOp",EDGE,"E13.31.0.1"),sQuery(id+"F0.wireOp",EDGE,"E13.31.0.2"),sQuery(id+"F0.wireOp",EDGE,"E13.31.0.3"),sQuery(id+"F0.wireOp",EDGE,"E13.32.0.0"),sQuery(id+"F0.wireOp",EDGE,"E13.32.0.1"),sQuery(id+"F0.wireOp",EDGE,"E13.32.0.2"),sQuery(id+"F0.wireOp",EDGE,"E13.32.0.3"),sQuery(id+"F0.wireOp",EDGE,"E13.33.0.0"),sQuery(id+"F0.wireOp",EDGE,"E13.33.0.1"),sQuery(id+"F0.wireOp",EDGE,"E13.33.0.2"),sQuery(id+"F0.wireOp",EDGE,"E13.33.0.3"),sQuery(id+"F0.wireOp",EDGE,"E13.34.0.0"),sQuery(id+"F0.wireOp",EDGE,"E13.34.0.1"),sQuery(id+"F0.wireOp",EDGE,"E13.34.0.2"),sQuery(id+"F0.wireOp",EDGE,"E13.34.0.3"),sQuery(id+"F0.wireOp",EDGE,"E13.35.0.0"),sQuery(id+"F0.wireOp",EDGE,"E13.35.0.1"),sQuery(id+"F0.wireOp",EDGE,"E13.35.0.2"),sQuery(id+"F0.wireOp",EDGE,"E13.35.0.3"),sQuery(id+"F0.wireOp",EDGE,"E13.36.0.0"),sQuery(id+"F0.wireOp",EDGE,"E13.36.0.1"),sQuery(id+"F0.wireOp",EDGE,"E13.36.0.2"),sQuery(id+"F0.wireOp",EDGE,"E13.36.0.3"),sQuery(id+"F0.wireOp",EDGE,"E13.37.0.0"),sQuery(id+"F0.wireOp",EDGE,"E13.37.0.1"),sQuery(id+"F0.wireOp",EDGE,"E13.37.0.2"),sQuery(id+"F0.wireOp",EDGE,"E13.37.0.3"),sQuery(id+"F0.wireOp",EDGE,"E13.38.0.0"),sQuery(id+"F0.wireOp",EDGE,"E13.38.0.1"),sQuery(id+"F0.wireOp",EDGE,"E13.38.0.2"),sQuery(id+"F0.wireOp",EDGE,"E13.38.0.3"),sQuery(id+"F0.wireOp",EDGE,"E13.39.0.0"),sQuery(id+"F0.wireOp",EDGE,"E13.39.0.1"),sQuery(id+"F0.wireOp",EDGE,"E13.39.0.2"),sQuery(id+"F0.wireOp",EDGE,"E13.39.0.3"),sQuery(id+"F0.wireOp",EDGE,"E14")])]});
            var Q1;
            Q1=makeQuery(id+"F3.opExtrude","SWEPT_FACE",FACE,{"disambiguationData":[OSD([sQuery(id+"F2.wireOp",EDGE,"E18")])]});
            mirror(context, id + "F10", {"operationType" : NewBodyOperationType.ADD, "entities" : qUnion([Q0]), "mirrorPlane" : qUnion([Q1])});
        }
        {
            var Q0;
            Q0=makeQuery(id+"F10.opPattern","COPY",EDGE,{"derivedFrom":makeQuery(id+"F3.opExtrude","CAP_EDGE",EDGE,{"disambiguationData":[OSD([sQuery(id+"F2.wireOp",EDGE,"E17.1")])],"isStart":false}),"instanceName":"1"});
            var Q1;
            {var subQ0=makeQuery(id+"F3.opExtrude","CAP_EDGE",EDGE,{"disambiguationData":[OSD([sQuery(id+"F2.wireOp",EDGE,"E17.0")])],"isStart":false});Q1=makeQuery(id+"F10.boolean.opBoolean","MERGE",EDGE,{"derivedFrom":[subQ0,makeQuery(id+"F10.opPattern","COPY",EDGE,{"derivedFrom":subQ0,"instanceName":"1"})]});}
            var Q2;
            Q2=makeQuery(id+"F3.opExtrude","CAP_EDGE",EDGE,{"disambiguationData":[OSD([sQuery(id+"F2.wireOp",EDGE,"E17.1")])],"isStart":false});
            var Q3;
            Q3=makeQuery(id+"F3.opExtrude","CAP_EDGE",EDGE,{"disambiguationData":[OSD([sQuery(id+"F2.wireOp",EDGE,"E17.1")])],"isStart":true});
            var Q4;
            {var subQ0=makeQuery(id+"F3.opExtrude","CAP_EDGE",EDGE,{"disambiguationData":[OSD([sQuery(id+"F2.wireOp",EDGE,"E17.0")])],"isStart":true});Q4=makeQuery(id+"F10.boolean.opBoolean","MERGE",EDGE,{"derivedFrom":[subQ0,makeQuery(id+"F10.opPattern","COPY",EDGE,{"derivedFrom":subQ0,"instanceName":"1"})]});}
            var Q5;
            Q5=makeQuery(id+"F10.opPattern","COPY",EDGE,{"derivedFrom":makeQuery(id+"F3.opExtrude","CAP_EDGE",EDGE,{"disambiguationData":[OSD([sQuery(id+"F2.wireOp",EDGE,"E17.1")])],"isStart":true}),"instanceName":"1"});
            fillet(context, id + "F11", {"entities" : qUnion([Q0, Q1, Q2, Q3, Q4, Q5]), "radius" : 0.5 * mm, "tangentPropagation" : true, "allowEdgeOverflow" : false});
        }
        {
            var Q0;
            Q0=makeQuery(id+"F10.opPattern","COPY",EDGE,{"derivedFrom":makeQuery(id+"F3.opExtrude","CAP_EDGE",EDGE,{"disambiguationData":[OSD([sQuery(id+"F2.wireOp",EDGE,"E15")])],"isStart":true}),"instanceName":"1"});
            var Q1;
            {var subQ0=makeQuery(id+"F3.opExtrude","CAP_EDGE",EDGE,{"disambiguationData":[OSD([sQuery(id+"F2.wireOp",EDGE,"E16")])],"isStart":true});Q1=makeQuery(id+"F10.boolean.opBoolean","MERGE",EDGE,{"derivedFrom":[subQ0,makeQuery(id+"F10.opPattern","COPY",EDGE,{"derivedFrom":subQ0,"instanceName":"1"})]});}
            var Q2;
            Q2=makeQuery(id+"F3.opExtrude","CAP_EDGE",EDGE,{"disambiguationData":[OSD([sQuery(id+"F2.wireOp",EDGE,"E15")])],"isStart":true});
            var Q3;
            Q3=makeQuery(id+"F3.opExtrude","CAP_EDGE",EDGE,{"disambiguationData":[OSD([sQuery(id+"F2.wireOp",EDGE,"E15")])],"isStart":false});
            var Q4;
            {var subQ0=makeQuery(id+"F3.opExtrude","CAP_EDGE",EDGE,{"disambiguationData":[OSD([sQuery(id+"F2.wireOp",EDGE,"E16")])],"isStart":false});Q4=makeQuery(id+"F10.boolean.opBoolean","MERGE",EDGE,{"derivedFrom":[subQ0,makeQuery(id+"F10.opPattern","COPY",EDGE,{"derivedFrom":subQ0,"instanceName":"1"})]});}
            var Q5;
            Q5=makeQuery(id+"F10.opPattern","COPY",EDGE,{"derivedFrom":makeQuery(id+"F3.opExtrude","CAP_EDGE",EDGE,{"disambiguationData":[OSD([sQuery(id+"F2.wireOp",EDGE,"E15")])],"isStart":false}),"instanceName":"1"});
            fillet(context, id + "F12", {"entities" : qUnion([Q0, Q1, Q2, Q3, Q4, Q5]), "radius" : 0.4 * mm, "tangentPropagation" : true, "allowEdgeOverflow" : false});
        }
    });
